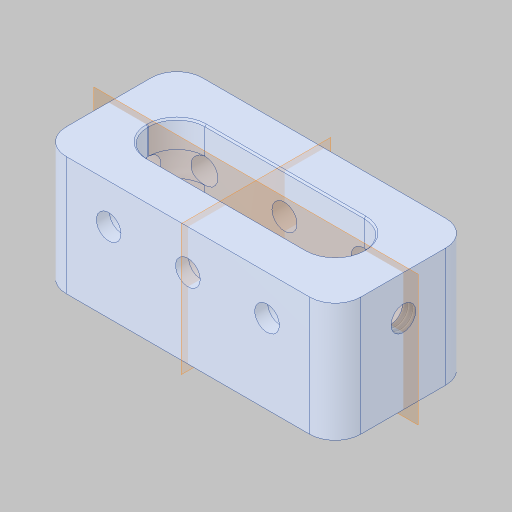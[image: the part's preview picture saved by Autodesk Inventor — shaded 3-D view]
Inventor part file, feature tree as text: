
AUTODESK INVENTOR PART (.ipt)
format: ipt  version: 2023.5 (Build 275446000, 446)  size: 450,560 bytes
history: native  units: in
note: dims shown in document units (in); Inventor stores cm internally (conversion verified against a paired STEP export)
features: sketch x4, hole x3, projected_geometry x2, extrude x1, chamfer x1
ambient origin geometry x8: Origin, YZ Plane, XZ Plane, XY Plane, X Axis, Y Axis, Z Axis, Center Point
bodies: Solid1 (feature_tree)
feature tree (11):
  extrude  "Extrusion1"  Depth=1.0in TaperAngle=0.0deg
  hole  "Hole1"  [1 undecoded]
  hole  "Hole2"  [1 undecoded]
  hole  "Hole3"  [1 undecoded]
  sketch  "Sketch1"  dims[d0=0.0625in d1=1.0in d2=0.0in]
  projected_geometry  "Projected Loop1"
  sketch  "Sketch2"  dims[d3=0.156in d4=0.38in d5=0.385in d6=0.25in d7=0.563in d8=1.0in d9=0.8108in]
  projected_geometry  "Projected Loop2"
  sketch  "Sketch3"  dims[d10=0.196in d11=0.5in d12=0.375in d13=0.25in d14=0.5635in d15=1.0in d16=0.8108in]
  sketch  "Sketch4"  dims[d17=0.156in d18=0.38in d19=0.385in d20=0.25in d21=0.563in d22=1.0in d23=0.8108in]
  chamfer  "Chamfer2"  [1 undecoded]
note: 4 required parameter values undecoded (feature->parameter linkage not recoverable at this tier; creation-order binding heuristic only, values carry confidence <= 0.55)
